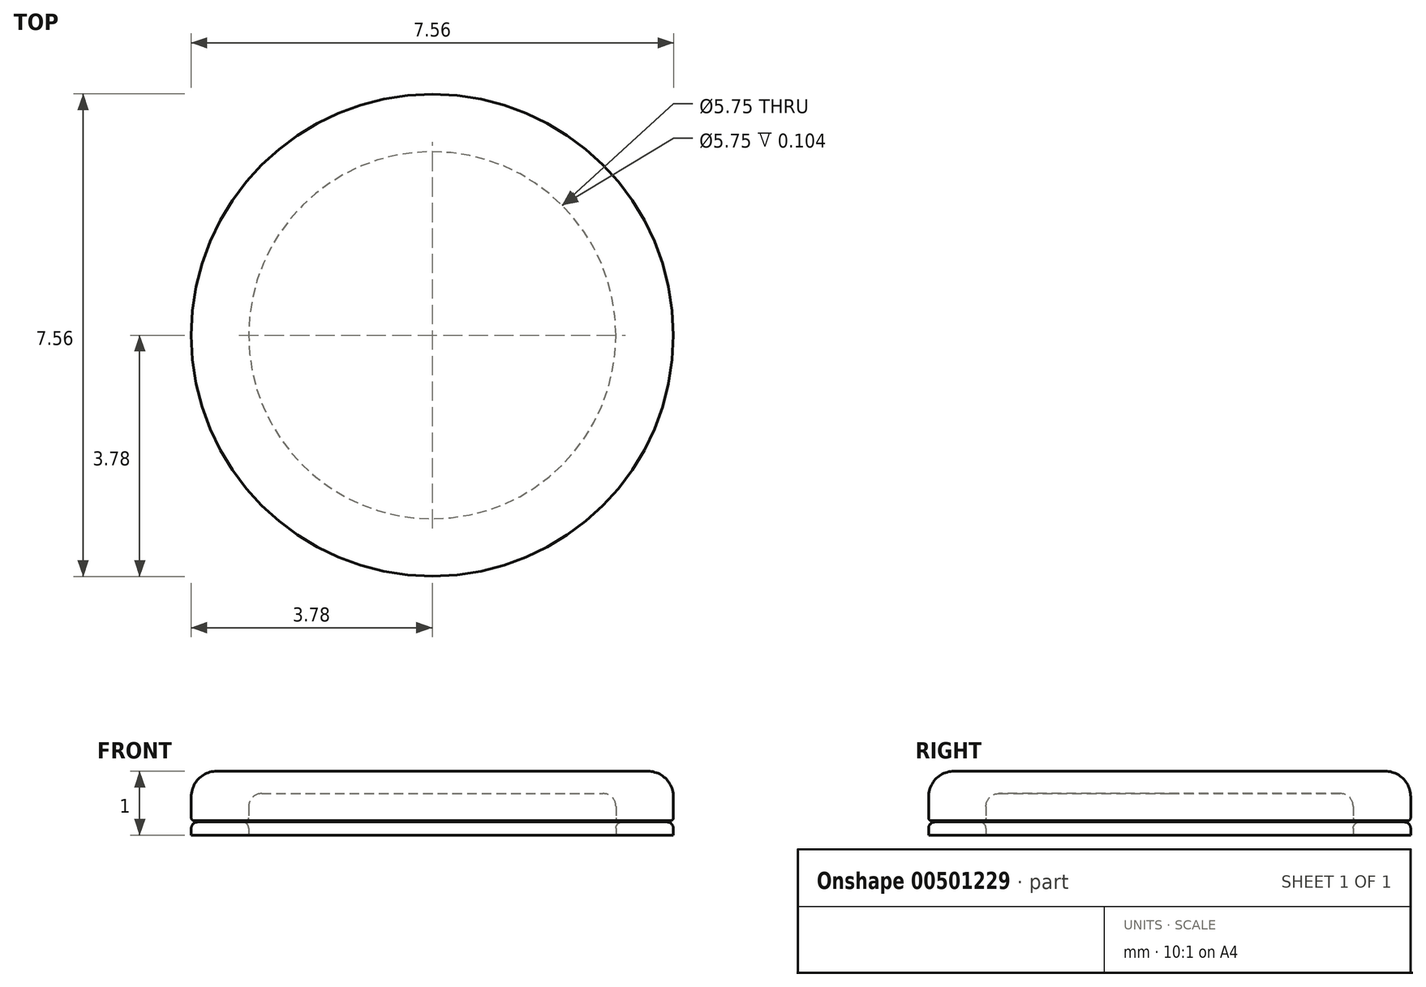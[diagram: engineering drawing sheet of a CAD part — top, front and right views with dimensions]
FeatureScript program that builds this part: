
annotation { "Feature Type Name" : "Feature", "Feature Type Description" : "" }
export const myFeature = defineFeature(function(context is Context, id is Id, definition is map)
    precondition{}
    {
        {
            var Q0;
            Q0=qCreatedBy(makeId("Front.planeOp"),FACE);
            var sketch = newSketch(context, id + "F0", { "sketchPlane" : qUnion([Q0])});
            skLineSegment(sketch, "E0", {"start": v(0, 0) * mm, "end": v(0, 1) * mm});
            skLineSegment(sketch, "E1", {"start": v(0, 1) * mm, "end": v(-3.37, 1) * mm});
            skPoint(sketch, "E2.visualSharp", {"position": v(-3.75, 1) * mm});
            skArc(sketch, "E2.filletArc", {"start": v(-3.37, 1) * mm, "mid": v(-3.66, 0.88) * mm, "end": v(-3.77, 0.6) * mm});
            skLineSegment(sketch, "E3", {"start": v(0, 0.65) * mm, "end": v(-2.67, 0.65) * mm});
            skPoint(sketch, "E4.visualSharp", {"position": v(-2.85, 0.65) * mm});
            skArc(sketch, "E4.filletArc", {"start": v(-2.67, 0.65) * mm, "mid": v(-2.82, 0.6) * mm, "end": v(-2.88, 0.45) * mm});
            skLineSegment(sketch, "E5", {"start": v(-3.28, 0) * mm, "end": v(-3.28, 1) * mm, "construction": true});
            skLineSegment(sketch, "E6", {"start": v(-3.28, 0.8) * mm, "end": v(-3.18, 0.8) * mm});
            skLineSegment(sketch, "E7", {"start": v(-3, 0.53) * mm, "end": v(-3, 0.48) * mm});
            skLineSegment(sketch, "E8", {"start": v(-3.02, 0.45) * mm, "end": v(-3.06, 0.4) * mm});
            skLineSegment(sketch, "E9.MirrorCS", {"start": v(-3.28, 0.8) * mm, "end": v(-3.38, 0.8) * mm});
            skLineSegment(sketch, "E10.MirrorCS", {"start": v(-3.56, 0.53) * mm, "end": v(-3.56, 0.48) * mm});
            skLineSegment(sketch, "E11.MirrorCS", {"start": v(-3.55, 0.45) * mm, "end": v(-3.5, 0.4) * mm});
            skLineSegment(sketch, "E12", {"start": v(-3.02, 0.56) * mm, "end": v(-3.14, 0.77) * mm});
            skLineSegment(sketch, "E13.MirrorCS", {"start": v(-3.55, 0.56) * mm, "end": v(-3.43, 0.77) * mm});
            skArc(sketch, "E14.filletArc", {"start": v(-3.06, 0.4) * mm, "mid": v(-3.07, 0.38) * mm, "end": v(-3.07, 0.37) * mm});
            skPoint(sketch, "E15.visualSharp", {"position": v(-3, 0.47) * mm});
            skArc(sketch, "E15.filletArc", {"start": v(-3.02, 0.45) * mm, "mid": v(-3.01, 0.47) * mm, "end": v(-3, 0.48) * mm});
            skPoint(sketch, "E16.visualSharp", {"position": v(-3, 0.55) * mm});
            skArc(sketch, "E16.filletArc", {"start": v(-3, 0.53) * mm, "mid": v(-3.01, 0.55) * mm, "end": v(-3.02, 0.56) * mm});
            skPoint(sketch, "E17.visualSharp", {"position": v(-3.15, 0.8) * mm});
            skArc(sketch, "E17.filletArc", {"start": v(-3.14, 0.77) * mm, "mid": v(-3.16, 0.8) * mm, "end": v(-3.18, 0.8) * mm});
            skPoint(sketch, "E18.visualSharp", {"position": v(-3.41, 0.8) * mm});
            skArc(sketch, "E18.filletArc", {"start": v(-3.38, 0.8) * mm, "mid": v(-3.4, 0.8) * mm, "end": v(-3.43, 0.77) * mm});
            skPoint(sketch, "E19.visualSharp", {"position": v(-3.56, 0.55) * mm});
            skArc(sketch, "E19.filletArc", {"start": v(-3.55, 0.56) * mm, "mid": v(-3.56, 0.55) * mm, "end": v(-3.56, 0.53) * mm});
            skPoint(sketch, "E20.visualSharp", {"position": v(-3.56, 0.47) * mm});
            skArc(sketch, "E20.filletArc", {"start": v(-3.56, 0.48) * mm, "mid": v(-3.56, 0.47) * mm, "end": v(-3.55, 0.45) * mm});
            skPoint(sketch, "E21.visualSharp", {"position": v(-3.5, 0.38) * mm});
            skArc(sketch, "E21.filletArc", {"start": v(-3.5, 0.37) * mm, "mid": v(-3.5, 0.38) * mm, "end": v(-3.5, 0.4) * mm});
            skArc(sketch, "E22.0", {"start": v(-3.08, 0.41) * mm, "mid": v(-3.1, 0.39) * mm, "end": v(-3.1, 0.37) * mm});
            skLineSegment(sketch, "E22.1", {"start": v(-3.04, 0.47) * mm, "end": v(-3.08, 0.41) * mm});
            skArc(sketch, "E22.2", {"start": v(-3.04, 0.47) * mm, "mid": v(-3.03, 0.48) * mm, "end": v(-3.03, 0.48) * mm});
            skLineSegment(sketch, "E22.3", {"start": v(-3.03, 0.53) * mm, "end": v(-3.03, 0.48) * mm});
            skArc(sketch, "E22.4", {"start": v(-3.03, 0.53) * mm, "mid": v(-3.03, 0.54) * mm, "end": v(-3.04, 0.55) * mm});
            skLineSegment(sketch, "E22.5", {"start": v(-3.04, 0.55) * mm, "end": v(-3.16, 0.76) * mm});
            skLineSegment(sketch, "E22.6", {"start": v(-3.53, 0.53) * mm, "end": v(-3.53, 0.48) * mm});
            skArc(sketch, "E22.7", {"start": v(-3.53, 0.48) * mm, "mid": v(-3.53, 0.48) * mm, "end": v(-3.53, 0.47) * mm});
            skLineSegment(sketch, "E22.8", {"start": v(-3.53, 0.47) * mm, "end": v(-3.48, 0.41) * mm});
            skArc(sketch, "E22.9", {"start": v(-3.47, 0.37) * mm, "mid": v(-3.47, 0.39) * mm, "end": v(-3.48, 0.41) * mm});
            skArc(sketch, "E22.10", {"start": v(-3.53, 0.55) * mm, "mid": v(-3.53, 0.54) * mm, "end": v(-3.53, 0.53) * mm});
            skLineSegment(sketch, "E22.11", {"start": v(-3.53, 0.55) * mm, "end": v(-3.4, 0.76) * mm});
            skArc(sketch, "E22.12", {"start": v(-3.38, 0.78) * mm, "mid": v(-3.4, 0.77) * mm, "end": v(-3.4, 0.76) * mm});
            skLineSegment(sketch, "E22.13", {"start": v(-3.3, 0.78) * mm, "end": v(-3.38, 0.78) * mm});
            skLineSegment(sketch, "E22.14", {"start": v(-3.3, 0.78) * mm, "end": v(-3.18, 0.78) * mm});
            skArc(sketch, "E22.15", {"start": v(-3.16, 0.76) * mm, "mid": v(-3.17, 0.77) * mm, "end": v(-3.18, 0.78) * mm});
            skLineSegment(sketch, "E23", {"start": v(-3.77, 0) * mm, "end": v(-2.88, 0) * mm});
            skLineSegment(sketch, "E24", {"start": v(-3.77, 0) * mm, "end": v(-3.77, 0.1) * mm});
            skLineSegment(sketch, "E25", {"start": v(-2.88, 0) * mm, "end": v(-2.88, 0.1) * mm});
            skLineSegment(sketch, "E26", {"start": v(-3.47, 0.37) * mm, "end": v(-3.47, 0.25) * mm});
            skLineSegment(sketch, "E27", {"start": v(-3.1, 0.37) * mm, "end": v(-3.1, 0.25) * mm});
            skLineSegment(sketch, "E28", {"start": v(-3.5, 0.37) * mm, "end": v(-3.5, 0.27) * mm});
            skLineSegment(sketch, "E29", {"start": v(-3.54, 0.22) * mm, "end": v(-3.72, 0.22) * mm});
            skLineSegment(sketch, "E30", {"start": v(-3.77, 0.27) * mm, "end": v(-3.77, 0.6) * mm});
            skLineSegment(sketch, "E31", {"start": v(-3.07, 0.37) * mm, "end": v(-3.07, 0.27) * mm});
            skLineSegment(sketch, "E32", {"start": v(-3.02, 0.22) * mm, "end": v(-2.93, 0.22) * mm});
            skLineSegment(sketch, "E33", {"start": v(-2.88, 0.27) * mm, "end": v(-2.88, 0.45) * mm});
            skLineSegment(sketch, "E34", {"start": v(-3.67, 0.2) * mm, "end": v(-3.52, 0.2) * mm});
            skLineSegment(sketch, "E35", {"start": v(-3.1, 0.2) * mm, "end": v(-3.47, 0.2) * mm});
            skLineSegment(sketch, "E36", {"start": v(-3.05, 0.2) * mm, "end": v(-2.97, 0.2) * mm});
            skPoint(sketch, "E37.visualSharp", {"position": v(-3.47, 0.2) * mm});
            skArc(sketch, "E37.filletArc", {"start": v(-3.52, 0.2) * mm, "mid": v(-3.48, 0.22) * mm, "end": v(-3.47, 0.25) * mm});
            skPoint(sketch, "E38.visualSharp", {"position": v(-3.1, 0.2) * mm});
            skArc(sketch, "E38.filletArc", {"start": v(-3.1, 0.25) * mm, "mid": v(-3.08, 0.22) * mm, "end": v(-3.05, 0.2) * mm});
            skPoint(sketch, "E39.visualSharp", {"position": v(-3.07, 0.22) * mm});
            skArc(sketch, "E39.filletArc", {"start": v(-3.07, 0.27) * mm, "mid": v(-3.06, 0.24) * mm, "end": v(-3.02, 0.22) * mm});
            skPoint(sketch, "E40.visualSharp", {"position": v(-2.88, 0.22) * mm});
            skArc(sketch, "E40.filletArc", {"start": v(-2.93, 0.22) * mm, "mid": v(-2.89, 0.24) * mm, "end": v(-2.88, 0.27) * mm});
            skPoint(sketch, "E41.visualSharp", {"position": v(-2.88, 0.2) * mm});
            skArc(sketch, "E41.filletArc", {"start": v(-2.88, 0.1) * mm, "mid": v(-2.9, 0.17) * mm, "end": v(-2.97, 0.2) * mm});
            skPoint(sketch, "E42.visualSharp", {"position": v(-3.77, 0.2) * mm});
            skArc(sketch, "E42.filletArc", {"start": v(-3.67, 0.2) * mm, "mid": v(-3.75, 0.17) * mm, "end": v(-3.77, 0.1) * mm});
            skPoint(sketch, "E43.visualSharp", {"position": v(-3.77, 0.22) * mm});
            skArc(sketch, "E43.filletArc", {"start": v(-3.77, 0.27) * mm, "mid": v(-3.76, 0.24) * mm, "end": v(-3.72, 0.22) * mm});
            skLineSegment(sketch, "E44", {"start": v(-3.52, 0.2) * mm, "end": v(-3.05, 0.2) * mm});
            skPoint(sketch, "E45.visualSharp", {"position": v(-3.5, 0.22) * mm});
            skArc(sketch, "E45.filletArc", {"start": v(-3.54, 0.22) * mm, "mid": v(-3.5, 0.24) * mm, "end": v(-3.5, 0.27) * mm});
            skLineSegment(sketch, "E46", {"start": v(-3.54, 0.22) * mm, "end": v(-3.02, 0.22) * mm});
            skSolve(sketch);
        }
        {
            var Q0;
            {var subQ5=sQuery(id+"F0.wireOp",EDGE,"E1");Q0=makeQuery(id+"F0.imprint","IMPRINT",FACE,{"disambiguationData":[TD([[makeQuery(id+"F0.imprint","IMPRINT",EDGE,{"derivedFrom":subQ5}),1.0]])]});}
            var Q1;
            Q1=makeQuery(id+"F0.imprint","IMPRINT",FACE,{"disambiguationData":[TD([[makeQuery(id+"F0.imprint","IMPRINT",EDGE,{"derivedFrom":sQuery(id+"F0.wireOp",EDGE,"E6")}),-1.0]])]});
            var Q2;
            Q2=makeQuery(id+"F0.imprint","IMPRINT",FACE,{"disambiguationData":[TD([[makeQuery(id+"F0.imprint","IMPRINT",EDGE,{"derivedFrom":sQuery(id+"F0.wireOp",EDGE,"E22.0")}),-1.0]])]});
            var Q3;
            Q3=makeQuery(id+"F0.imprint","IMPRINT",FACE,{"disambiguationData":[TD([[makeQuery(id+"F0.imprint","IMPRINT",EDGE,{"derivedFrom":sQuery(id+"F0.wireOp",EDGE,"E23")}),1.0]])]});
            var Q4;
            Q4=sQuery(id+"F0.wireOp",EDGE,"E0");
            revolve(context, id + "F1", {"entities" : qUnion([Q0, Q1, Q2, Q3]), "axis" : qUnion([Q4]), "revolveType" : RevolveType.FULL});
        }
    });
